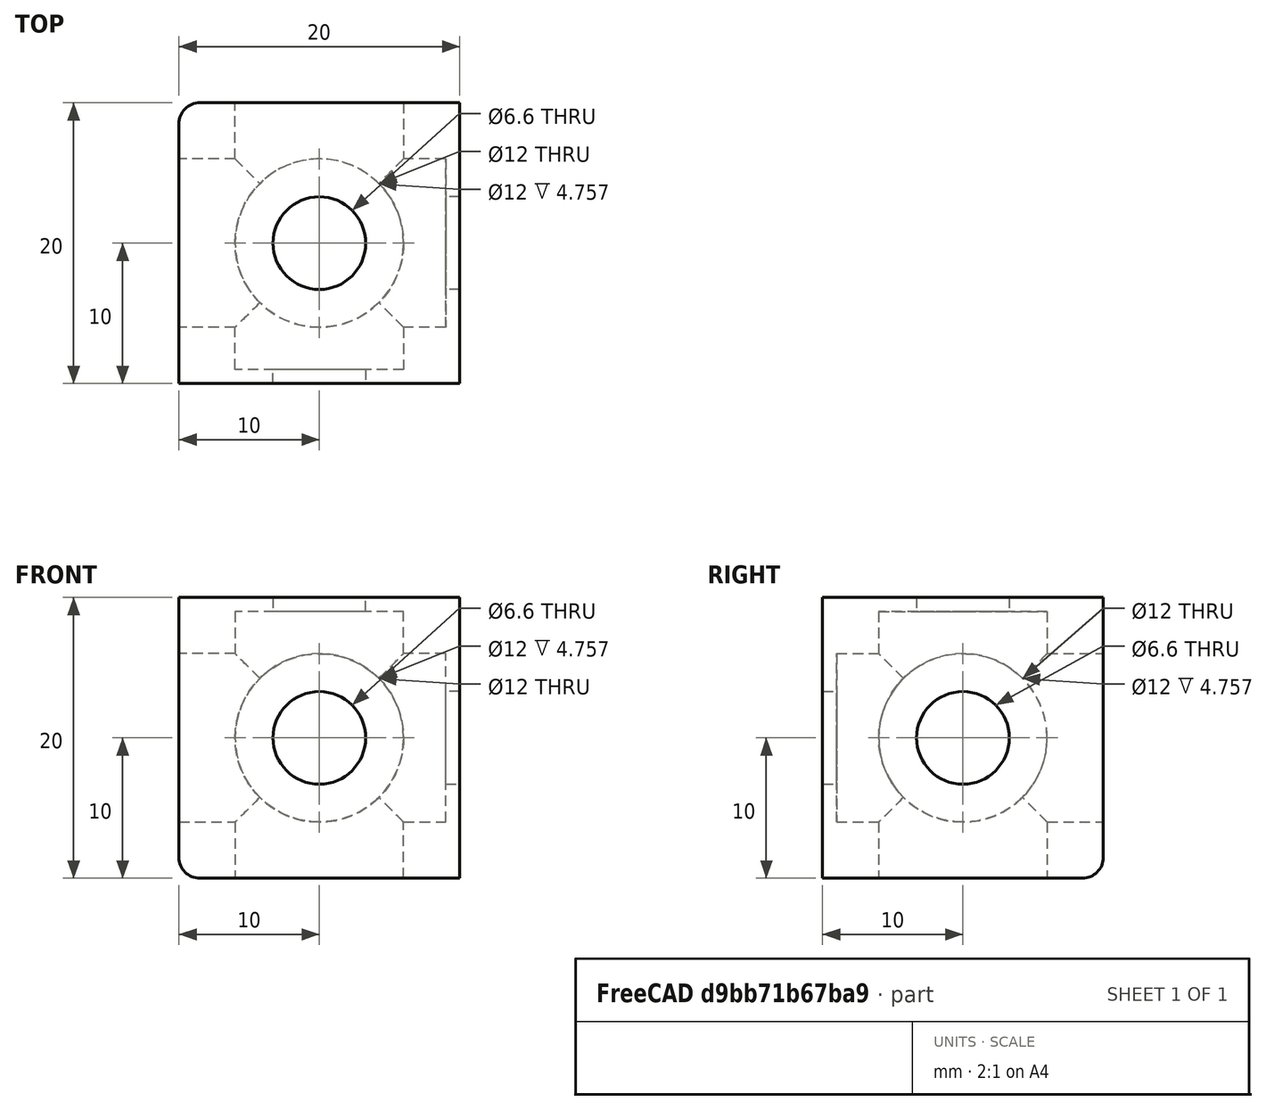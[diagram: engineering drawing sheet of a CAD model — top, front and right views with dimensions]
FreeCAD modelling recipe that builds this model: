
FCSTD DOCUMENT  (FreeCAD 0.21R0.21.1)
Label: EdgeConnectorCube_20x20
License: All rights reserved
LicenseURL: http://en.wikipedia.org/wiki/All_rights_reserved
objects: Part::Cylinder×6, Part::Box×1, Part::MultiFuse×1, Part::Cut×1, Part::Fillet×1
note: 10 computed .brp shape members not serialized (recipe doc carries the construction recipe); baked Part::Feature solids carry a one-line shape summary decoded from their .brp

FEATURE [Part::Box] Box  label="Cube"
  AttacherType = Attacher::AttachEngine3D
  Height = 20
  Length = 20
  Width = 20
FEATURE [Part::Cylinder] Cylinder
  Angle = 360
  AttacherType = Attacher::AttachEngine3D
  FirstAngle = 0
  Height = 20
  Placement = pos=(10,10,0) rot=(0,0,1;0rad)
  Radius = 3.3
  SecondAngle = 0
FEATURE [Part::Cylinder] Cylinder001
  Angle = 360
  AttacherType = Attacher::AttachEngine3D
  FirstAngle = 0
  Height = 20
  Placement = pos=(10,20,10) rot=(1,0,0;1.5708rad)
  Radius = 3.3
  SecondAngle = 0
FEATURE [Part::Cylinder] Cylinder002
  Angle = 360
  AttacherType = Attacher::AttachEngine3D
  FirstAngle = 0
  Height = 20
  Placement = pos=(0,10,10) rot=(0,1,0;1.5708rad)
  Radius = 3.3
  SecondAngle = 0
FEATURE [Part::Cylinder] Cylinder003
  Angle = 360
  AttacherType = Attacher::AttachEngine3D
  FirstAngle = 0
  Height = 19
  Placement = pos=(0,10,10) rot=(0,1,0;1.5708rad)
  Radius = 6
  SecondAngle = 0
FEATURE [Part::Cylinder] Cylinder004
  Angle = 360
  AttacherType = Attacher::AttachEngine3D
  FirstAngle = 0
  Height = 19
  Placement = pos=(10,10,0) rot=(0,0,1;0rad)
  Radius = 6
  SecondAngle = 0
FEATURE [Part::Cylinder] Cylinder005
  Angle = 360
  AttacherType = Attacher::AttachEngine3D
  FirstAngle = 0
  Height = 19
  Placement = pos=(10,20,10) rot=(1,0,0;1.5708rad)
  Radius = 6
  SecondAngle = 0
FEATURE [Part::MultiFuse] Fusion
  Shapes = -> [Cylinder005,Cylinder,Cylinder001,Cylinder002,Cylinder003,Cylinder004]
FEATURE [Part::Cut] Cut
  Base = -> Box
  Tool = -> Fusion
FEATURE [Part::Fillet] Fillet  label="20x20ConnectorCube"
  Base = -> Cut
  Edges = 3 edges r=1.5: [Edge3,Edge4,Edge13]
